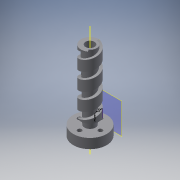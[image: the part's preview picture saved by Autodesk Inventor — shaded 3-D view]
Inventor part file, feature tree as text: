
AUTODESK INVENTOR PART (.ipt)
format: ipt  version: 2017 (Build 210142000, 142)  size: 253,440 bytes
history: native  units: mm
features: sketch x6, extrude x5, plane x1, other x1, helix x1, revolve x1
ambient origin geometry x8: Origin, YZ Plane, XZ Plane, XY Plane, X Axis, Y Axis, Z Axis, Center Point
bodies: Solid1 (feature_tree)
feature tree (15):
  extrude  "Extrusion1"  Depth=3.0mm
  extrude  "Extrusion2"  Depth=24.0mm
  extrude  "Extrusion3"  Depth=7.0mm
  extrude  "Extrusion5"  Depth=13.0mm
  plane  "Work Plane1"
  extrude  "Extrusion8"  Depth=6.5mm
  sketch  "Sketch9"  dims[d34=12.0mm d44=6.0mm d45=4.5mm d46=0.0mm d61=5.0mm d62=5.0mm d63=12.5mm d64=50.0mm d65=40.0mm d66=0.174533mm d67=90.0deg d68=90.0deg d69=0.0mm d70=0.0mm d71=90.0deg]
  other  "Work Axis1"
  helix  "Coil2"  [1 undecoded]
  revolve  "Revolution2"  [1 undecoded]
  sketch  "Sketch1"  dims[d0=7.5mm d1=3.0mm]
  sketch  "Sketch2"  dims[d2=80.0mm d4=360.0deg d6=24.0mm]
  sketch  "Sketch3"  dims[d7=7.0mm d8=0.0mm d9=13.0mm]
  sketch  "Sketch5"  dims[d10=1.0mm d11=0.0mm d12=13.0mm]
  sketch  "Sketch8"  dims[d13=50.0mm d14=0.0mm d25=6.5mm d26=6.0mm d27=0.0mm]
note: 2 required parameter values undecoded (feature->parameter linkage not recoverable at this tier; creation-order binding heuristic only, values carry confidence <= 0.55)